# Revit family: IRO
name_source: partatom
category: Luminaires
units: mm (PartAtom-declared; Revit-internal decimal feet)

## family parameters
Cote de connecteur circulaire = Utiliser le diamètre
Couper avec des vides une fois chargée = Oui
Hôte = Face
Numéro OmniClass = 23.80.70.11.17
Partagée = Oui
Point de calcul de pièce = Oui
Source d'éclairage = Oui
Titre OmniClass = Specialized Lighting by Location or Use
Type d'élément = Normal

## types (14) — shared parameters
Angle de l'inclinaison = 60.00°
Emettre la visibilité des formes dans le rendu = Non
Emettre à partir de la largeur du rectangle = 610 mm
Emettre à partir de la longueur du rectangle = 1219 mm
Fabricant = Résistex
Filtre de couleur = 16777215
Garantie = 5 ans
Gradation des changements de température de couleur de lampe = <Aucun>
Image du type = <Aucun>
Indice de charge = Eclairage
Matériau corps = Alu blanc
Matériau diffuseur = PC Transparent
Modèle = Iro
Nombre pôles = 1
Tension = 230 V
URL = https://www.resistex-sa.com
Épaisseur 2 = 2 mm  [stored 0.00656168 ft]
zero-valued in all types: Elévation par défaut

## per-type parameters (varying)
| type | Charge apparente | Commentaires relatifs à la puissance | Coût | Description | Distance bord corps | Fichier de distribution photométrique | IK | IP | Largeur | Largeur 2 | Longueur | Longueur 2 | Épaisseur |
| 621441 | 29 VA | 28.9W | 57.5 $ | Encastré tertiaire équipé d'une platine LED SMD, efficacité lumineuse de 143lm/W | 28 mm  [stored 0.0918635 ft] | 621441.ies | 04 | 40 | 595 mm  [stored 1.9521 ft] | 551 mm  [stored 1.80774 ft] | 595 mm  [stored 1.9521 ft] | 551 mm  [stored 1.80774 ft] | 30 mm  [stored 0.0984252 ft] |
| 621442 | 29 VA | 28.5W | 57.5 $ | Encastré tertiaire équipé d'une platine LED SMD, efficacité lumineuse de 148lm/W | 28 mm  [stored 0.0918635 ft] | 621442.ies | 04 | 40 | 595 mm  [stored 1.9521 ft] | 551 mm  [stored 1.80774 ft] | 595 mm  [stored 1.9521 ft] | 551 mm  [stored 1.80774 ft] | 30 mm  [stored 0.0984252 ft] |
| 621443 | 29 VA | 28.9W | 75 $ | Encastré tertiaire équipé d'une platine LED SMD, efficacité lumineuse de 143lm/W | 28 mm  [stored 0.0918635 ft] | 621443.ies | 04 | 40 | 595 mm  [stored 1.9521 ft] | 551 mm  [stored 1.80774 ft] | 595 mm  [stored 1.9521 ft] | 551 mm  [stored 1.80774 ft] | 30 mm  [stored 0.0984252 ft] |
| 621444 | 29 VA | 28.5W | 75 $ | Encastré tertiaire équipé d'une platine LED SMD, efficacité lumineuse de 148lm/W | 28 mm  [stored 0.0918635 ft] | 621444.ies | 04 | 40 | 595 mm  [stored 1.9521 ft] | 551 mm  [stored 1.80774 ft] | 595 mm  [stored 1.9521 ft] | 551 mm  [stored 1.80774 ft] | 30 mm  [stored 0.0984252 ft] |
| 621456 | 31 VA | 29.9W | 62.5 $ | Encastré tertiaire équipé d'une platine LED SMD, efficacité lumineuse de 145lm/W | 24 mm  [stored 0.0787402 ft] | 621456.ies | 04 | 40 | 595 mm  [stored 1.9521 ft] | 551 mm  [stored 1.80774 ft] | 595 mm  [stored 1.9521 ft] | 551 mm  [stored 1.80774 ft] | 26 mm |
| 621448 | 31 VA | 29.9W | 52.5 $ | Encastré tertiaire équipé d'une platine LED SMD, efficacité lumineuse de 142lm/W | 28 mm  [stored 0.0918635 ft] | 621448.ies | 04 | 40 | 1195 mm  [stored 3.9206 ft] | 1133 mm | 295 mm  [stored 0.967848 ft] | 233 mm | 30 mm  [stored 0.0984252 ft] |
| 621449 | 31 VA | 29.9W | 52.5 $ | Encastré tertiaire équipé d'une platine LED SMD, efficacité lumineuse de 145lm/W | 28 mm  [stored 0.0918635 ft] | 621449.ies | 04 | 40 | 1195 mm  [stored 3.9206 ft] | 1133 mm | 295 mm  [stored 0.967848 ft] | 233 mm | 30 mm  [stored 0.0984252 ft] |
| 621424 | 28 VA | 27.6W | 125 $ | Encastré tertiaire équipé d'une platine LED SMD, efficacité lumineuse de 140.5lm/W | 28 mm  [stored 0.0918635 ft] | 621424.ies | 04 | 40 | 595 mm  [stored 1.9521 ft] | 504 mm | 595 mm  [stored 1.9521 ft] | 504 mm | 30 mm  [stored 0.0984252 ft] |
| 621425 | 28 VA | 27.7W | 125 $ | Encastré tertiaire équipé d'une platine LED SMD, efficacité lumineuse de 140.8lm/W | 28 mm  [stored 0.0918635 ft] | 621425.ies | 04 | 40 | 595 mm  [stored 1.9521 ft] | 504 mm | 595 mm  [stored 1.9521 ft] | 504 mm | 30 mm  [stored 0.0984252 ft] |
| 621431 | 31 VA | 29.9W | 142.5 $ | Encastré tertiaire équipé d'une platine LED SMD, efficacité lumineuse de 148lm/W | 28 mm  [stored 0.0918635 ft] | 621431.ies | 04 | 40 | 595 mm  [stored 1.9521 ft] | 504 mm | 595 mm  [stored 1.9521 ft] | 504 mm | 30 mm  [stored 0.0984252 ft] |
| 621436 | 29 VA | 28.9W | 142.5 $ | Encastré tertiaire équipé d'une platine LED SMD, efficacité lumineuse de 143lm/W | 28 mm  [stored 0.0918635 ft] | 621436.ies | 04 | 40 | 595 mm  [stored 1.9521 ft] | 504 mm | 595 mm  [stored 1.9521 ft] | 504 mm | 30 mm  [stored 0.0984252 ft] |
| 621432 | 29 VA | 28.5W | 250 $ | Encastré tertiaire équipé d'une platine LED SMD, efficacité lumineuse de 148lm/W | 28 mm  [stored 0.0918635 ft] | 621432.ies | 04 | 40 | 595 mm  [stored 1.9521 ft] | 504 mm | 595 mm  [stored 1.9521 ft] | 504 mm | 30 mm  [stored 0.0984252 ft] |
| 621437 | 29 VA | 28.9W | 250 $ | Encastré tertiaire équipé d'une platine LED SMD, efficacité lumineuse de 143lm/W | 28 mm  [stored 0.0918635 ft] | 621437.ies | 04 | 40 | 595 mm  [stored 1.9521 ft] | 504 mm | 595 mm  [stored 1.9521 ft] | 504 mm | 30 mm  [stored 0.0984252 ft] |
| 621430 | 33 VA | 29.9W | 117.5 $ | Encastré tertiaire équipé d'une platine LED SMD, efficacité lumineuse de 142lm/W | 28 mm  [stored 0.0918635 ft] | 621430.ies | 07 | 65 | 595 mm  [stored 1.9521 ft] | 551 mm  [stored 1.80774 ft] | 595 mm  [stored 1.9521 ft] | 551 mm  [stored 1.80774 ft] | 30 mm  [stored 0.0984252 ft] |

note: [stored X ft] marks values corroborated as IEEE doubles in the binary element streams (Revit-internal decimal feet)
